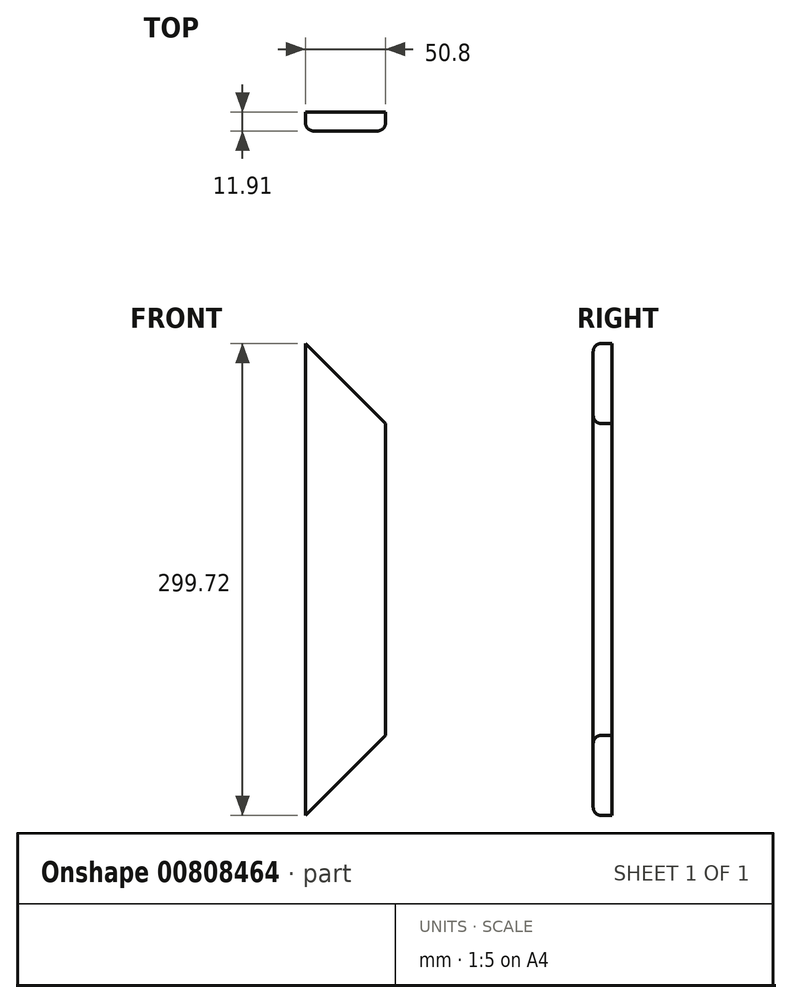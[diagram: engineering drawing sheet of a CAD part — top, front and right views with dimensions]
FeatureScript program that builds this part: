
annotation { "Feature Type Name" : "Feature", "Feature Type Description" : "" }
export const myFeature = defineFeature(function(context is Context, id is Id, definition is map)
    precondition{}
    {
        {
            var Q0;
            Q0=qCreatedBy(makeId("Front.planeOp"),FACE);
            var sketch = newSketch(context, id + "F0", { "sketchPlane" : qUnion([Q0])});
            skLineSegment(sketch, "E0", {"start": v(-59.36, 63.49) * mm, "end": v(-59.36, 38.09) * mm});
            skLineSegment(sketch, "E1", {"start": v(-59.36, 38.09) * mm, "end": v(-33.96, 38.09) * mm});
            skLineSegment(sketch, "E2", {"start": v(-33.96, 38.09) * mm, "end": v(-59.36, 63.49) * mm});
            skSolve(sketch);
        }
        {
            var Q0;
            Q0=qCreatedBy(makeId("Front.planeOp"),FACE);
            var sketch = newSketch(context, id + "F1", { "sketchPlane" : qUnion([Q0])});
            skLineSegment(sketch, "E3", {"start": v(-25.4, 149.86) * mm, "end": v(-25.4, -149.86) * mm});
            skLineSegment(sketch, "E4", {"start": v(-25.4, -149.86) * mm, "end": v(25.4, -99.06) * mm});
            skLineSegment(sketch, "E5", {"start": v(25.4, -99.06) * mm, "end": v(25.4, 99.06) * mm});
            skLineSegment(sketch, "E6", {"start": v(25.4, 99.06) * mm, "end": v(-25.4, 149.86) * mm});
            skSolve(sketch);
        }
        {
            var Q0;
            Q0 = qSketchRegion(id + "F1", true);
            extrude(context, id + "F2", {"entities" : qUnion([Q0]), "depth" : 11.9 * mm, "offsetDistance" : 25.4 * mm});
        }
        {
            var Q0;
            Q0=makeQuery(id+"F2.opExtrude","CAP_EDGE",EDGE,{"disambiguationData":[OSD([sQuery(id+"F1.wireOp",EDGE,"E5")])],"isStart":false});
            fillet(context, id + "F3", {"entities" : qUnion([Q0]), "radius" : 5.08 * mm, "tangentPropagation" : true, "allowEdgeOverflow" : false});
        }
        {
            var Q0;
            Q0=makeQuery(id+"F2.opExtrude","CAP_EDGE",EDGE,{"disambiguationData":[OSD([sQuery(id+"F1.wireOp",EDGE,"E3")])],"isStart":false});
            fillet(context, id + "F4", {"entities" : qUnion([Q0]), "radius" : 5.08 * mm, "tangentPropagation" : true, "allowEdgeOverflow" : false});
        }
    });
